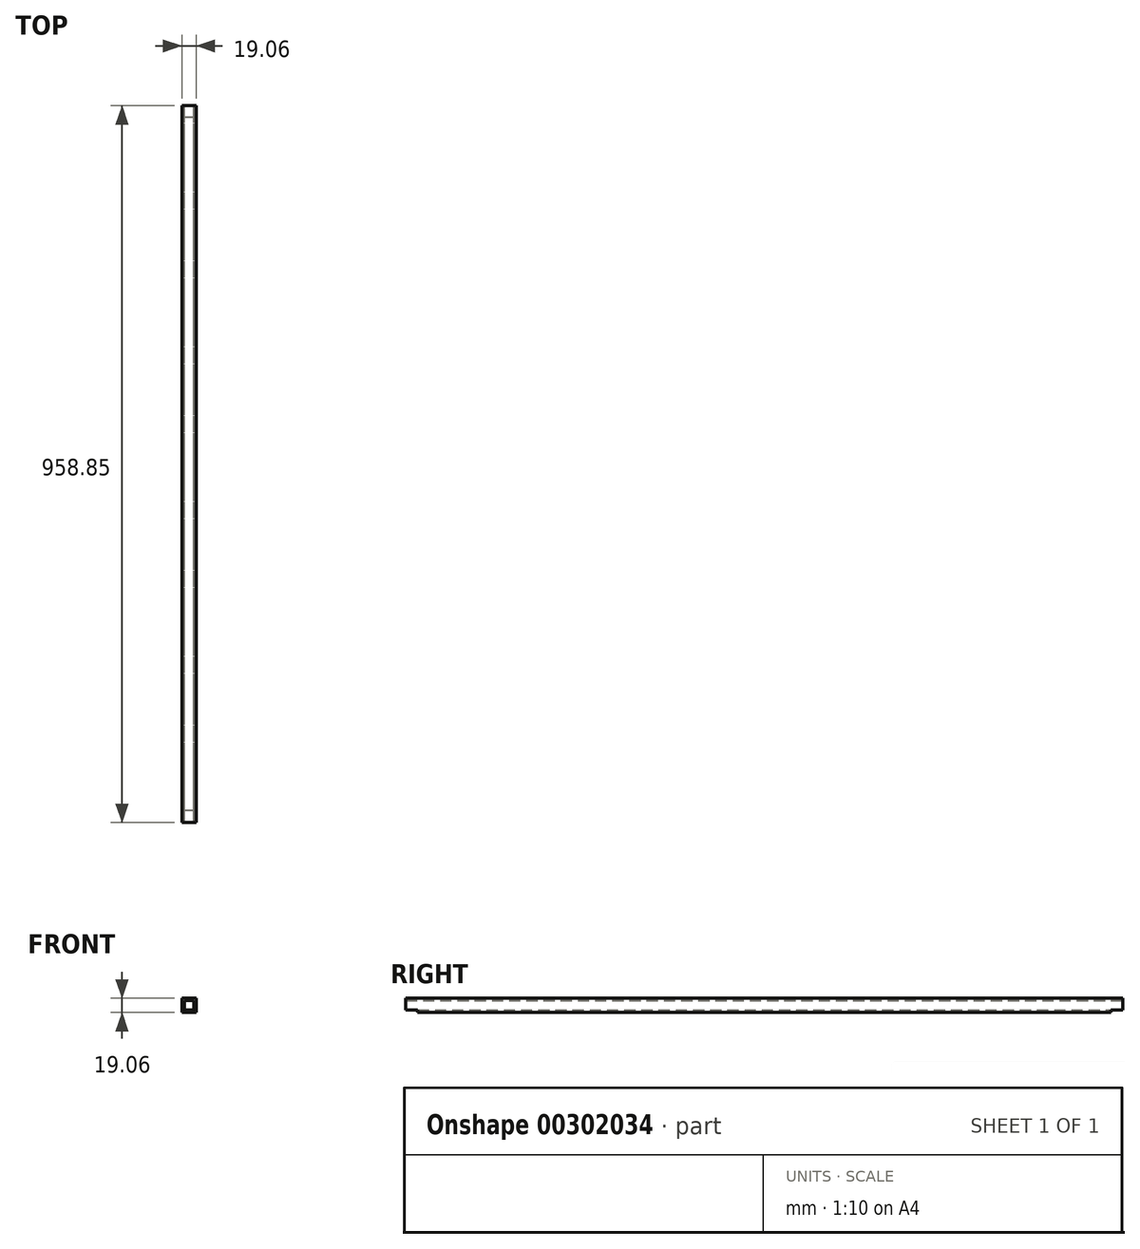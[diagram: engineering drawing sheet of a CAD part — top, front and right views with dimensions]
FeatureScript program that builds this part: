
annotation { "Feature Type Name" : "Feature", "Feature Type Description" : "" }
export const myFeature = defineFeature(function(context is Context, id is Id, definition is map)
    precondition{}
    {
        {
            var Q0;
            Q0=qCreatedBy(makeId("Front.planeOp"),FACE);
            var sketch = newSketch(context, id + "F0", { "sketchPlane" : qUnion([Q0])});
            skLineSegment(sketch, "E0.bottom", {"start": v(9.53, 9.53) * mm, "end": v(-9.53, 9.52) * mm});
            skLineSegment(sketch, "E0.top", {"start": v(9.53, -9.52) * mm, "end": v(-9.53, -9.53) * mm});
            skLineSegment(sketch, "E0.left", {"start": v(9.52, 9.53) * mm, "end": v(9.53, -9.52) * mm});
            skLineSegment(sketch, "E0.right", {"start": v(-9.53, 9.52) * mm, "end": v(-9.53, -9.53) * mm});
            skPoint(sketch, "E0.middle", {"position": v(0, 0) * mm});
            skLineSegment(sketch, "E1.bottom", {"start": v(6.35, 6.35) * mm, "end": v(-6.35, 6.35) * mm});
            skLineSegment(sketch, "E1.top", {"start": v(6.35, -6.35) * mm, "end": v(-6.35, -6.35) * mm});
            skLineSegment(sketch, "E1.left", {"start": v(6.35, 6.35) * mm, "end": v(6.35, -6.35) * mm});
            skLineSegment(sketch, "E1.right", {"start": v(-6.35, 6.35) * mm, "end": v(-6.35, -6.35) * mm});
            skSolve(sketch);
        }
        {
            var Q0;
            Q0 = qSketchRegion(id + "F0", true);
            extrude(context, id + "F1", {"entities" : qUnion([Q0]), "depth" : 958.85 * mm});
        }
        {
            var Q0;
            Q0=makeQuery(id+"F1.opExtrude","SWEPT_FACE",FACE,{"disambiguationData":[OSD([sQuery(id+"F0.wireOp",EDGE,"E0.right")])]});
            var sketch = newSketch(context, id + "F2", { "sketchPlane" : qUnion([Q0])});
            skLineSegment(sketch, "E2.bottom", {"start": v(0, -9.53) * mm, "end": v(15.88, -9.53) * mm});
            skLineSegment(sketch, "E2.top", {"start": v(0, -6.35) * mm, "end": v(15.88, -6.35) * mm});
            skLineSegment(sketch, "E2.left", {"start": v(0, -9.53) * mm, "end": v(0, -6.35) * mm});
            skLineSegment(sketch, "E2.right", {"start": v(15.88, -9.53) * mm, "end": v(15.88, -6.35) * mm});
            skLineSegment(sketch, "E3.bottom", {"start": v(958.85, -9.53) * mm, "end": v(942.98, -9.53) * mm});
            skLineSegment(sketch, "E3.top", {"start": v(958.85, -6.35) * mm, "end": v(942.98, -6.35) * mm});
            skLineSegment(sketch, "E3.left", {"start": v(958.85, -9.53) * mm, "end": v(958.85, -6.35) * mm});
            skLineSegment(sketch, "E3.right", {"start": v(942.98, -9.53) * mm, "end": v(942.98, -6.35) * mm});
            skSolve(sketch);
        }
        {
            var Q0;
            Q0 = qSketchRegion(id + "F2", true);
            extrude(context, id + "F3", {"entities" : qUnion([Q0]), "operationType" : NewBodyOperationType.REMOVE, "oppositeDirection" : true, "depth" : 19.05 * mm});
        }
    });
